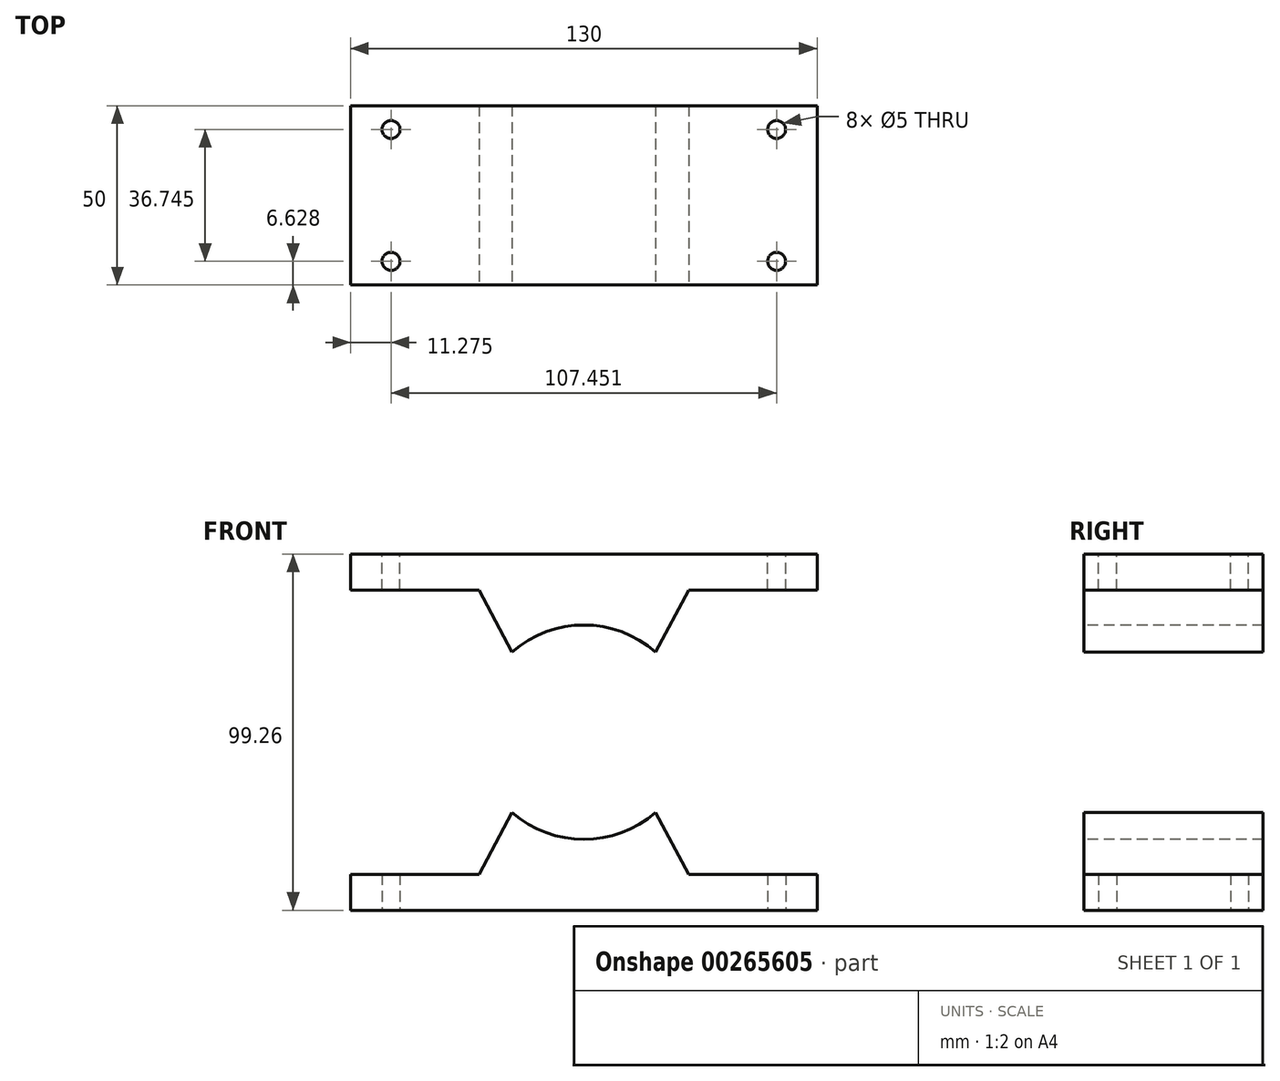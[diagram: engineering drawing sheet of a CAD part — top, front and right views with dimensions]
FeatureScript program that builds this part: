
annotation { "Feature Type Name" : "Feature", "Feature Type Description" : "" }
export const myFeature = defineFeature(function(context is Context, id is Id, definition is map)
    precondition{}
    {
        {
            var Q0;
            Q0=qCreatedBy(makeId("Front.planeOp"),FACE);
            var sketch = newSketch(context, id + "F0", { "sketchPlane" : qUnion([Q0])});
            skLineSegment(sketch, "E0", {"start": v(-75, 0) * mm, "end": v(75, 0) * mm, "construction": true});
            skPoint(sketch, "E1.orphan", {"position": v(0, 0) * mm});
            skLineSegment(sketch, "E2.bottom", {"start": v(65, 49.63) * mm, "end": v(-65, 49.63) * mm});
            skLineSegment(sketch, "E2.top", {"start": v(65, 39.63) * mm, "end": v(29.2, 39.63) * mm});
            skLineSegment(sketch, "E2.left", {"start": v(65, 49.63) * mm, "end": v(65, 39.63) * mm});
            skLineSegment(sketch, "E2.right", {"start": v(-65, 49.63) * mm, "end": v(-65, 39.63) * mm});
            skPoint(sketch, "E3", {"position": v(0, 49.63) * mm});
            skLineSegment(sketch, "E4.trimOffspring", {"start": v(-29.2, 39.63) * mm, "end": v(-65, 39.63) * mm});
            skLineSegment(sketch, "E5", {"start": v(-29.2, 39.63) * mm, "end": v(-19.98, 22.33) * mm});
            skLineSegment(sketch, "E6", {"start": v(29.2, 39.63) * mm, "end": v(19.98, 22.33) * mm});
            skArc(sketch, "E7", {"start": v(19.98, 22.33) * mm, "mid": v(0, 29.88) * mm, "end": v(-19.98, 22.33) * mm});
            skSolve(sketch);
        }
        {
            var Q0;
            Q0=makeQuery(id+"F0.imprint","IMPRINT",FACE,{"disambiguationData":[TD([[makeQuery(id+"F0.imprint","IMPRINT",EDGE,{"derivedFrom":sQuery(id+"F0.wireOp",EDGE,"E2.bottom")}),1.0]])]});
            extrude(context, id + "F1", {"entities" : qUnion([Q0]), "oppositeDirection" : true, "depth" : 50 * mm});
        }
        {
            var Q0;
            Q0=makeQuery(id+"F1.opExtrude","SWEPT_FACE",FACE,{"disambiguationData":[OSD([sQuery(id+"F0.wireOp",EDGE,"E2.bottom")])]});
            var sketch = newSketch(context, id + "F2", { "sketchPlane" : qUnion([Q0])});
            skLineSegment(sketch, "E8", {"start": v(0, 50) * mm, "end": v(0, 0) * mm, "construction": true});
            skLineSegment(sketch, "E9.bottom", {"start": v(53.73, 43.37) * mm, "end": v(-53.73, 43.37) * mm, "construction": true});
            skLineSegment(sketch, "E9.top", {"start": v(53.73, 6.63) * mm, "end": v(-53.73, 6.63) * mm, "construction": true});
            skLineSegment(sketch, "E9.left", {"start": v(53.73, 43.37) * mm, "end": v(53.73, 6.63) * mm, "construction": true});
            skLineSegment(sketch, "E9.right", {"start": v(-53.73, 43.37) * mm, "end": v(-53.73, 6.63) * mm, "construction": true});
            skPoint(sketch, "E9.middle", {"position": v(0, 25) * mm});
            skCircle(sketch, "E10", {"center": v(-53.73, 43.37) * mm, "radius": 2.5 * mm});
            skCircle(sketch, "E11", {"center": v(53.73, 43.37) * mm, "radius": 2.5 * mm});
            skCircle(sketch, "E12", {"center": v(53.73, 6.63) * mm, "radius": 2.5 * mm});
            skCircle(sketch, "E13", {"center": v(-53.73, 6.63) * mm, "radius": 2.5 * mm});
            skSolve(sketch);
        }
        {
            var Q0;
            Q0=makeQuery(id+"F2.imprint","IMPRINT",FACE,{"disambiguationData":[TD([[makeQuery(id+"F2.imprint","IMPRINT",EDGE,{"derivedFrom":sQuery(id+"F2.wireOp",EDGE,"E10")}),1.0]])]});
            var Q1;
            Q1=makeQuery(id+"F2.imprint","IMPRINT",FACE,{"disambiguationData":[TD([[makeQuery(id+"F2.imprint","IMPRINT",EDGE,{"derivedFrom":sQuery(id+"F2.wireOp",EDGE,"E13")}),1.0]])]});
            var Q2;
            Q2=makeQuery(id+"F2.imprint","IMPRINT",FACE,{"disambiguationData":[TD([[makeQuery(id+"F2.imprint","IMPRINT",EDGE,{"derivedFrom":sQuery(id+"F2.wireOp",EDGE,"E11")}),1.0]])]});
            var Q3;
            Q3=makeQuery(id+"F2.imprint","IMPRINT",FACE,{"disambiguationData":[TD([[makeQuery(id+"F2.imprint","IMPRINT",EDGE,{"derivedFrom":sQuery(id+"F2.wireOp",EDGE,"E12")}),1.0]])]});
            var Q4;
            Q4=sQuery(id+"F2.wireOp",EDGE,"E10");
            var Q5;
            Q5=sQuery(id+"F2.wireOp",EDGE,"E13");
            var Q6;
            Q6=sQuery(id+"F2.wireOp",EDGE,"E11");
            var Q7;
            Q7=sQuery(id+"F2.wireOp",EDGE,"E12");
            extrude(context, id + "F3", {"entities" : qUnion([Q0, Q1, Q2, Q3]), "operationType" : NewBodyOperationType.REMOVE, "surfaceEntities" : qUnion([Q4, Q5, Q6, Q7]), "oppositeDirection" : true, "depth" : 10 * mm});
        }
        {
            var Q0;
            Q0=makeQuery(id+"F1.opExtrude","SWEPT_BODY",BODY,{"disambiguationData":[OSD([sQuery(id+"F0.wireOp",EDGE,"E2.bottom"),sQuery(id+"F0.wireOp",EDGE,"E2.top"),sQuery(id+"F0.wireOp",EDGE,"E2.left"),sQuery(id+"F0.wireOp",EDGE,"E2.right"),sQuery(id+"F0.wireOp",EDGE,"E4.trimOffspring"),sQuery(id+"F0.wireOp",EDGE,"E5"),sQuery(id+"F0.wireOp",EDGE,"E6"),sQuery(id+"F0.wireOp",EDGE,"E7")])]});
            var Q1;
            Q1=qCreatedBy(makeId("Top.planeOp"),FACE);
            mirror(context, id + "F4", {"entities" : qUnion([Q0]), "mirrorPlane" : qUnion([Q1])});
        }
    });
